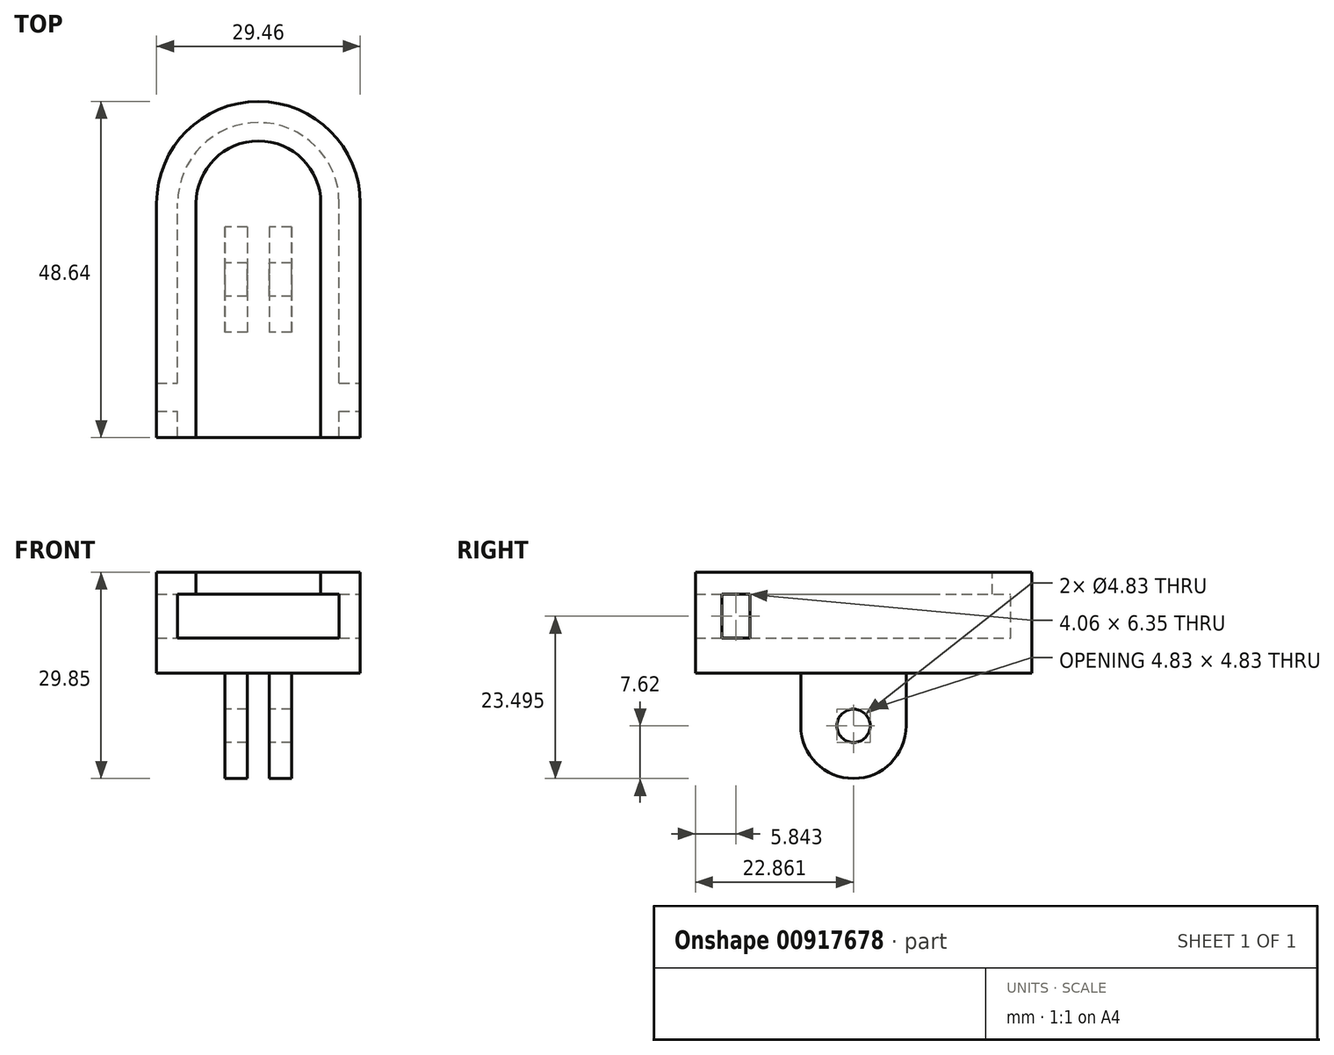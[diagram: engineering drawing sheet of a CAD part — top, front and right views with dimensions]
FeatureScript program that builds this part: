
annotation { "Feature Type Name" : "Feature", "Feature Type Description" : "" }
export const myFeature = defineFeature(function(context is Context, id is Id, definition is map)
    precondition{}
    {
        {
            var Q0;
            Q0=qCreatedBy(makeId("Front.planeOp"),FACE);
            var sketch = newSketch(context, id + "F0", { "sketchPlane" : qUnion([Q0])});
            skLineSegment(sketch, "E0", {"start": v(0, 0) * mm, "end": v(-14.73, 0) * mm});
            skLineSegment(sketch, "E1", {"start": v(-14.73, 0) * mm, "end": v(-14.73, 14.6) * mm});
            skLineSegment(sketch, "E2", {"start": v(-14.73, 14.6) * mm, "end": v(-9.02, 14.6) * mm});
            skLineSegment(sketch, "E3", {"start": v(-9.02, 14.6) * mm, "end": v(-9.02, 11.43) * mm});
            skLineSegment(sketch, "E4", {"start": v(-9.02, 11.43) * mm, "end": v(-11.68, 11.43) * mm});
            skLineSegment(sketch, "E5", {"start": v(-11.68, 11.43) * mm, "end": v(-11.68, 5.08) * mm});
            skLineSegment(sketch, "E6", {"start": v(-11.68, 5.08) * mm, "end": v(0, 5.08) * mm});
            skLineSegment(sketch, "E7", {"start": v(0, 5.08) * mm, "end": v(0, 0) * mm});
            skLineSegment(sketch, "E8", {"start": v(0, 23.48) * mm, "end": v(0, -10.29) * mm});
            skSolve(sketch);
        }
        {
            var Q0;
            {var subQ0=sQuery(id+"F0.wireOp",EDGE,"E0");Q0=makeQuery(id+"F0.imprint","IMPRINT",FACE,{"disambiguationData":[TD([[makeQuery(id+"F0.imprint","IMPRINT",EDGE,{"derivedFrom":subQ0}),-1.0]])]});}
            var Q1;
            Q1 = qSketchRegion(id + "F0", true);
            var Q2;
            Q2=sQuery(id+"F0.wireOp",EDGE,"E8");
            revolve(context, id + "F1", {"surfaceOperationType" : NewSurfaceOperationType.NEW, "entities" : qUnion([Q0, Q1]), "axis" : qUnion([Q2]), "revolveType" : RevolveType.ONE_DIRECTION, "angle" : 180 * degree});
        }
        {
            var Q0;
            Q0=makeQuery(id+"F1.opRevolve","CAP_FACE",FACE,{"disambiguationData":[OSD([sQuery(id+"F0.wireOp",EDGE,"E0"),sQuery(id+"F0.wireOp",EDGE,"E1"),sQuery(id+"F0.wireOp",EDGE,"E2"),sQuery(id+"F0.wireOp",EDGE,"E3"),sQuery(id+"F0.wireOp",EDGE,"E4"),sQuery(id+"F0.wireOp",EDGE,"E5"),sQuery(id+"F0.wireOp",EDGE,"E6"),sQuery(id+"F0.wireOp",EDGE,"E8")])],"isStart":true});
            extrude(context, id + "F2", {"entities" : qUnion([Q0]), "operationType" : NewBodyOperationType.ADD, "depth" : 33.9 * mm, "offsetDistance" : 25.4 * mm});
        }
        {
            var Q0;
            {var subQ0=sQuery(id+"F0.wireOp",EDGE,"E1");Q0=makeQuery(id+"F2.opExtrude","SWEPT_FACE",FACE,{"disambiguationData":[OSD([subQ0]),TDD([makeQuery(id+"F1.opRevolve","CAP_EDGE",EDGE,{"disambiguationData":[OSD([subQ0])],"isStart":false})])]});}
            var sketch = newSketch(context, id + "F3", { "sketchPlane" : qUnion([Q0])});
            skLineSegment(sketch, "E9.0", {"start": v(-30.1, 5.08) * mm, "end": v(-26.04, 5.08) * mm});
            skLineSegment(sketch, "E10.0", {"start": v(-30.1, 11.43) * mm, "end": v(-26.04, 11.43) * mm});
            skLineSegment(sketch, "E11", {"start": v(-30.1, 11.43) * mm, "end": v(-30.1, 5.08) * mm});
            skLineSegment(sketch, "E12", {"start": v(-26.04, 11.43) * mm, "end": v(-26.04, 5.08) * mm});
            skPoint(sketch, "E13.orphan", {"position": v(-33.9, 11.43) * mm});
            skPoint(sketch, "E14.orphan", {"position": v(-33.9, 5.08) * mm});
            skPoint(sketch, "E15.orphan", {"position": v(0, 11.43) * mm});
            skPoint(sketch, "E16.orphan", {"position": v(0, 5.08) * mm});
            skSolve(sketch);
        }
        {
            var Q0;
            Q0=makeQuery(id+"F3.imprint","IMPRINT",FACE,{"disambiguationData":[TD([[makeQuery(id+"F3.imprint","IMPRINT",EDGE,{"derivedFrom":sQuery(id+"F3.wireOp",EDGE,"E9.0")}),1.0]])]});
            extrude(context, id + "F4", {"entities" : qUnion([Q0]), "operationType" : NewBodyOperationType.REMOVE, "endBound" : BoundingType.THROUGH_ALL, "oppositeDirection" : true, "depth" : 25.4 * mm, "offsetDistance" : 25.4 * mm});
        }
        {
            var Q0;
            Q0=qCreatedBy(makeId("Right.planeOp"),FACE);
            var sketch = newSketch(context, id + "F5", { "sketchPlane" : qUnion([Q0])});
            skLineSegment(sketch, "E17.bottom", {"start": v(-3.43, 0) * mm, "end": v(-18.67, 0) * mm});
            skLineSegment(sketch, "E17.top", {"start": v(-11.05, -15.24) * mm, "end": v(-11.05, -15.24) * mm});
            skLineSegment(sketch, "E17.left", {"start": v(-3.43, 0) * mm, "end": v(-3.43, -7.62) * mm});
            skLineSegment(sketch, "E17.right", {"start": v(-18.67, 0) * mm, "end": v(-18.67, -7.62) * mm});
            skPoint(sketch, "E18.visualSharp", {"position": v(-18.67, -15.24) * mm});
            skArc(sketch, "E18.filletArc", {"start": v(-18.67, -7.62) * mm, "mid": v(-16.44, -13) * mm, "end": v(-11.05, -15.24) * mm});
            skPoint(sketch, "E19.visualSharp", {"position": v(-3.43, -15.24) * mm});
            skArc(sketch, "E19.filletArc", {"start": v(-11.05, -15.24) * mm, "mid": v(-5.66, -13) * mm, "end": v(-3.43, -7.62) * mm});
            skCircle(sketch, "E20", {"center": v(-11.05, -7.62) * mm, "radius": 2.41 * mm});
            skSolve(sketch);
        }
        {
            var Q0;
            Q0=makeQuery(id+"F5.imprint","IMPRINT",FACE,{"disambiguationData":[TD([[makeQuery(id+"F5.imprint","IMPRINT",EDGE,{"derivedFrom":sQuery(id+"F5.wireOp",EDGE,"E17.bottom")}),1.0]])]});
            extrude(context, id + "F6", {"entities" : qUnion([Q0]), "operationType" : NewBodyOperationType.ADD, "endBound" : BoundingType.SYMMETRIC, "depth" : 9.65 * mm, "offsetDistance" : 25.4 * mm});
        }
        {
            var Q0;
            Q0=makeQuery(id+"F6.opExtrude","SWEPT_FACE",FACE,{"disambiguationData":[OSD([sQuery(id+"F5.wireOp",EDGE,"E17.right")])]});
            var sketch = newSketch(context, id + "F7", { "sketchPlane" : qUnion([Q0])});
            skLineSegment(sketch, "E21.bottom", {"start": v(-1.59, 0) * mm, "end": v(1.59, 0) * mm});
            skLineSegment(sketch, "E21.top", {"start": v(-1.59, -17.78) * mm, "end": v(1.59, -17.78) * mm});
            skLineSegment(sketch, "E21.left", {"start": v(-1.59, 0) * mm, "end": v(-1.59, -17.78) * mm});
            skLineSegment(sketch, "E21.right", {"start": v(1.59, 0) * mm, "end": v(1.59, -17.78) * mm});
            skSolve(sketch);
        }
        {
            var Q0;
            {var subQ0=sQuery(id+"F7.wireOp",EDGE,"E21.bottom");Q0=makeQuery(id+"F7.imprint","IMPRINT",FACE,{"disambiguationData":[TD([[makeQuery(id+"F7.imprint","IMPRINT",EDGE,{"derivedFrom":subQ0}),1.0]])]});}
            var Q1;
            {var subQ0=sQuery(id+"F7.wireOp",EDGE,"E21.top");Q1=makeQuery(id+"F7.imprint","IMPRINT",FACE,{"disambiguationData":[TD([[makeQuery(id+"F7.imprint","IMPRINT",EDGE,{"derivedFrom":subQ0}),1.0]])]});}
            extrude(context, id + "F8", {"entities" : qUnion([Q0, Q1]), "operationType" : NewBodyOperationType.REMOVE, "oppositeDirection" : true, "depth" : 25.4 * mm, "offsetDistance" : 25.4 * mm});
        }
    });
